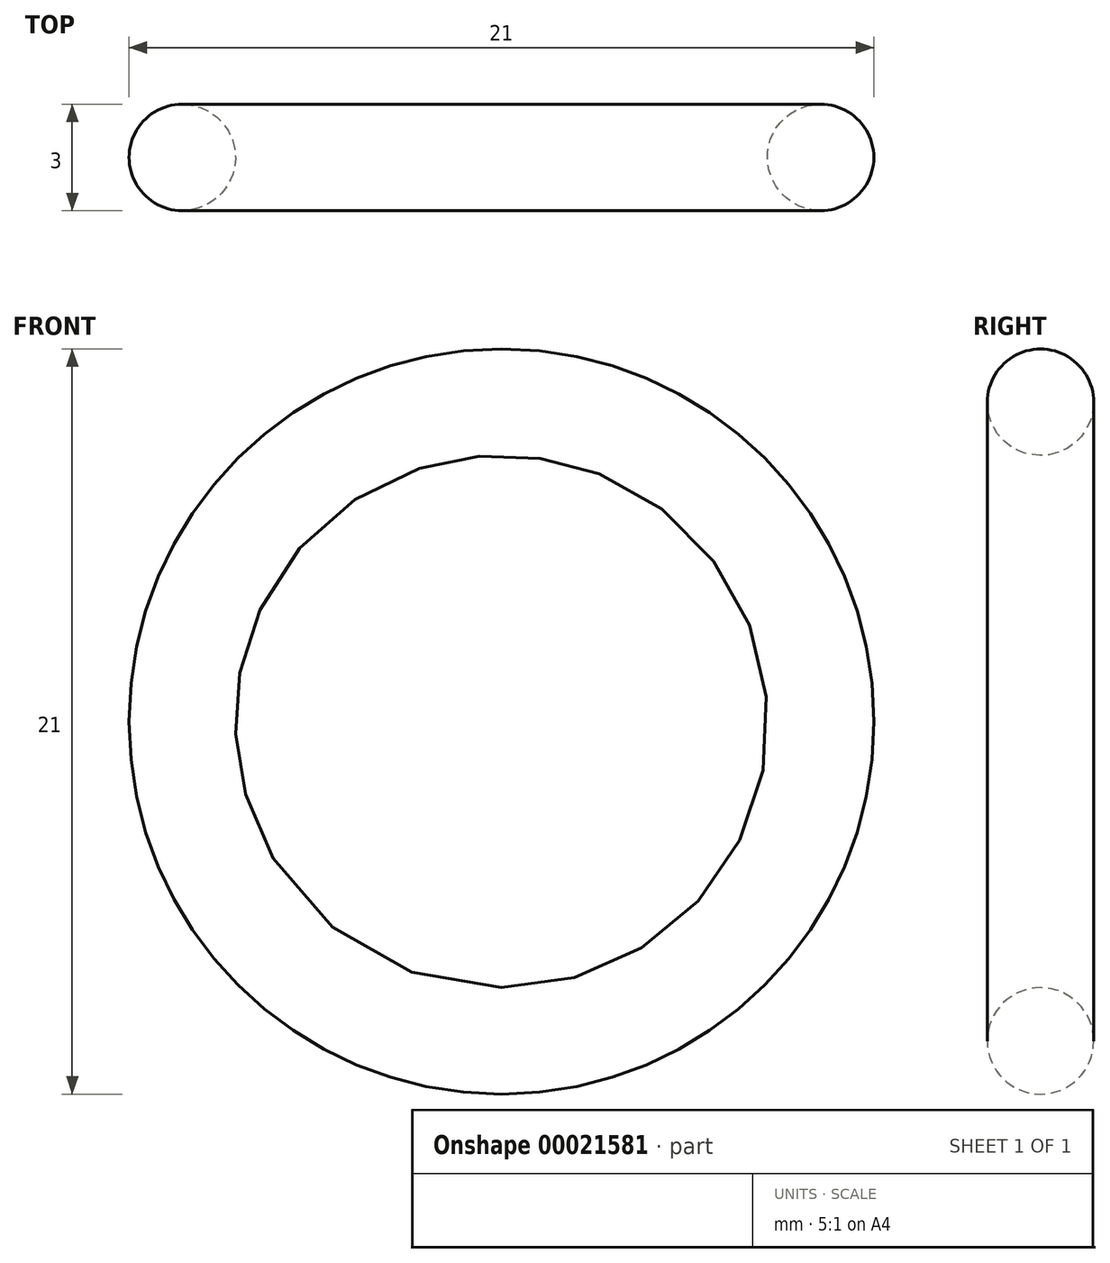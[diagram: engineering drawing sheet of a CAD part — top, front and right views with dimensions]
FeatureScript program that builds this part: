
annotation { "Feature Type Name" : "Feature", "Feature Type Description" : "" }
export const myFeature = defineFeature(function(context is Context, id is Id, definition is map)
    precondition{}
    {
        {
            var Q0;
            Q0=qCreatedBy(makeId("Top.planeOp"),FACE);
            var sketch = newSketch(context, id + "F0", { "sketchPlane" : qUnion([Q0])});
            skCircle(sketch, "E0", {"center": v(9, 0) * mm, "radius": 1.5 * mm});
            skLineSegment(sketch, "E1", {"start": v(0, 0) * mm, "end": v(0, 27) * mm, "construction": true});
            skSolve(sketch);
        }
        {
            var Q0;
            Q0 = qSketchRegion(id + "F0", true);
            var Q1;
            Q1=sQuery(id+"F0.wireOp",EDGE,"E1");
            revolve(context, id + "F1", {"entities" : qUnion([Q0]), "axis" : qUnion([Q1]), "revolveType" : RevolveType.FULL});
        }
    });
